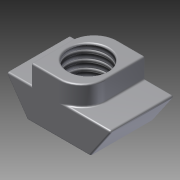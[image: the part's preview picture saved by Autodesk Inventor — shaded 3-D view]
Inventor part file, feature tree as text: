
AUTODESK INVENTOR PART (.ipt)
format: ipt  version: 2011 (Build 150239000, 239)  size: 173,056 bytes
history: native  units: in
note: dims shown in document units (in); Inventor stores cm internally (conversion verified against a paired STEP export)
features: extrude x2, fillet x2, sketch x2, thread x1
ambient origin geometry x8: Origin, YZ Plane, XZ Plane, XY Plane, X Axis, Y Axis, Z Axis, Center Point
bodies: Solid1 (feature_tree)
feature tree (7):
  extrude  "Extrusion1"  Depth=0.675in
  extrude  "Extrusion2"  Depth=0.1375in
  fillet  "Fillet1"  Radius=0.325in
  fillet  "Fillet2"  Radius=0.125in
  thread  "Thread1"  [1 undecoded]
  sketch  "Sketch1"  dims[d0=0.2in d1=0.675in]
  sketch  "Sketch2"  dims[d2=0.4in d3=0.1375in d4=0.325in d5=0.125in d6=0.1625in d7=0.4in d8=0.0in d9=0.25in d10=1.0in d11=0.0in d12=0.15in d13=0.01in d14=1.0in d15=0.0in]
note: 1 required parameter value undecoded (feature->parameter linkage not recoverable at this tier; creation-order binding heuristic only, values carry confidence <= 0.55)
